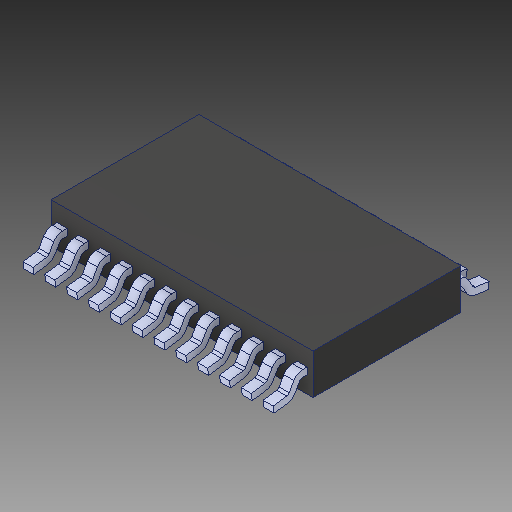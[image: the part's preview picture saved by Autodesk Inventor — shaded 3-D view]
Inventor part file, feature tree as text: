
AUTODESK INVENTOR PART (.ipt)
format: ipt  version: 2018 (Build 220112000, 112)  size: 299,008 bytes
history: native  units: in
note: dims shown in document units (in); Inventor stores cm internally (conversion verified against a paired STEP export)
features: mirror x1
ambient origin geometry x8: Origin, YZ Plane, XZ Plane, XY Plane, X Axis, Y Axis, Z Axis, Center Point
bodies: Solid1 (feature_tree)
feature tree (1):
  mirror  "Mirror1"
